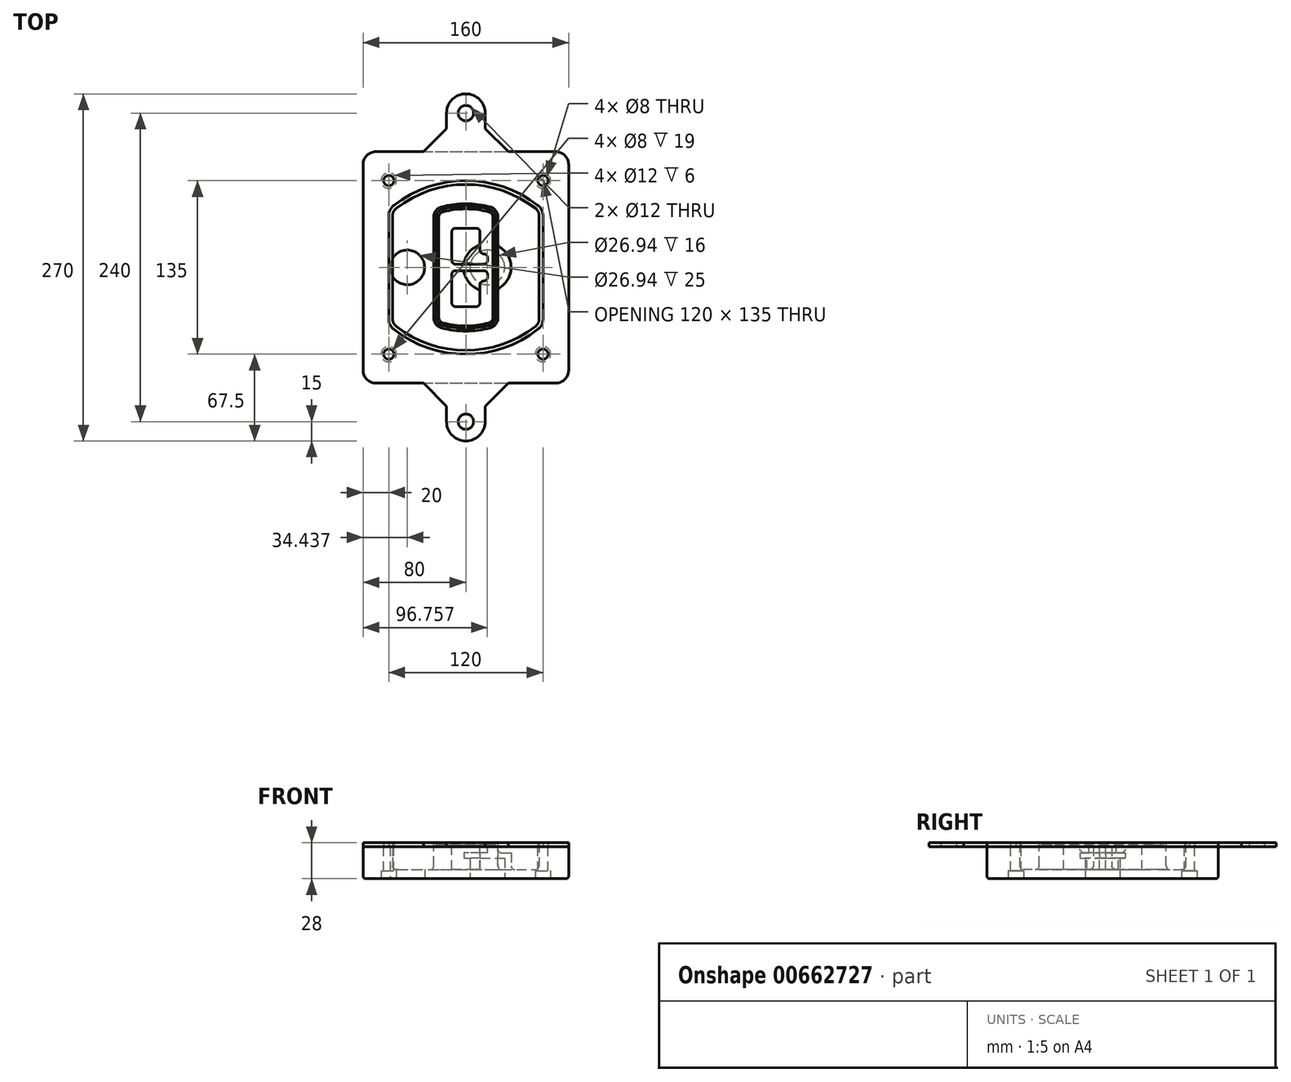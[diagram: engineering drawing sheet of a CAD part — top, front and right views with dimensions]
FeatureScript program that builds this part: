
annotation { "Feature Type Name" : "Feature", "Feature Type Description" : "" }
export const myFeature = defineFeature(function(context is Context, id is Id, definition is map)
    precondition{}
    {
        {
            var Q0;
            Q0=qCreatedBy(makeId("Top.planeOp"),FACE);
            var sketch = newSketch(context, id + "F0", { "sketchPlane" : qUnion([Q0])});
            skPoint(sketch, "E0.rect.middle", {"position": v(0, 0) * mm});
            skLineSegment(sketch, "E1.bottom", {"start": v(-70, -90) * mm, "end": v(70, -90) * mm});
            skLineSegment(sketch, "E1.top", {"start": v(-70, 90) * mm, "end": v(70, 90) * mm});
            skLineSegment(sketch, "E1.left", {"start": v(-80, -80) * mm, "end": v(-80, 80) * mm});
            skLineSegment(sketch, "E1.right", {"start": v(80, -80) * mm, "end": v(80, 80) * mm});
            skLineSegment(sketch, "E2", {"start": v(-80, 90) * mm, "end": v(80, -90) * mm, "construction": true});
            skLineSegment(sketch, "E3", {"start": v(80, 90) * mm, "end": v(-80, -90) * mm, "construction": true});
            skCircle(sketch, "E4", {"center": v(-60, 67.5) * mm, "radius": 4 * mm});
            skCircle(sketch, "E5", {"center": v(60, 67.5) * mm, "radius": 4 * mm});
            skCircle(sketch, "E6", {"center": v(60, -67.5) * mm, "radius": 4 * mm});
            skCircle(sketch, "E7", {"center": v(-60, -67.5) * mm, "radius": 4 * mm});
            skLineSegment(sketch, "E8", {"start": v(-60, 67.5) * mm, "end": v(60, 67.5) * mm, "construction": true});
            skLineSegment(sketch, "E9", {"start": v(60, 67.5) * mm, "end": v(60, -67.5) * mm, "construction": true});
            skLineSegment(sketch, "E10", {"start": v(60, -67.5) * mm, "end": v(-60, -67.5) * mm, "construction": true});
            skLineSegment(sketch, "E11", {"start": v(-60, -67.5) * mm, "end": v(-60, 67.5) * mm, "construction": true});
            skLineSegment(sketch, "E12", {"start": v(-60, 40.3) * mm, "end": v(-60, -40.3) * mm});
            skLineSegment(sketch, "E13", {"start": v(60, 40.3) * mm, "end": v(60, -40.3) * mm});
            skArc(sketch, "E14", {"start": v(56.15, 48.18) * mm, "mid": v(0, 67.5) * mm, "end": v(-56.15, 48.18) * mm});
            skArc(sketch, "E15", {"start": v(-56.15, -48.18) * mm, "mid": v(0, -67.5) * mm, "end": v(56.15, -48.18) * mm});
            skLineSegment(sketch, "E16", {"start": v(-60, 0) * mm, "end": v(60, 0) * mm, "construction": true});
            skPoint(sketch, "E17.visualSharp", {"position": v(-60, -45) * mm});
            skArc(sketch, "E17.filletArc", {"start": v(-60, -40.3) * mm, "mid": v(-58.99, -44.68) * mm, "end": v(-56.15, -48.18) * mm});
            skPoint(sketch, "E18.visualSharp", {"position": v(-60, 45) * mm});
            skArc(sketch, "E18.filletArc", {"start": v(-56.15, 48.18) * mm, "mid": v(-58.99, 44.68) * mm, "end": v(-60, 40.3) * mm});
            skPoint(sketch, "E19.visualSharp", {"position": v(60, 45) * mm});
            skArc(sketch, "E19.filletArc", {"start": v(60, 40.3) * mm, "mid": v(58.99, 44.68) * mm, "end": v(56.15, 48.18) * mm});
            skPoint(sketch, "E20.visualSharp", {"position": v(60, -45) * mm});
            skArc(sketch, "E20.filletArc", {"start": v(56.15, -48.18) * mm, "mid": v(58.99, -44.68) * mm, "end": v(60, -40.3) * mm});
            skPoint(sketch, "E21.visualSharp", {"position": v(-80, 90) * mm});
            skArc(sketch, "E21.filletArc", {"start": v(-70, 90) * mm, "mid": v(-77.07, 87.07) * mm, "end": v(-80, 80) * mm});
            skPoint(sketch, "E22.visualSharp", {"position": v(80, 90) * mm});
            skArc(sketch, "E22.filletArc", {"start": v(80, 80) * mm, "mid": v(77.07, 87.07) * mm, "end": v(70, 90) * mm});
            skPoint(sketch, "E23.visualSharp", {"position": v(80, -90) * mm});
            skArc(sketch, "E23.filletArc", {"start": v(70, -90) * mm, "mid": v(77.07, -87.07) * mm, "end": v(80, -80) * mm});
            skPoint(sketch, "E24.visualSharp", {"position": v(-80, -90) * mm});
            skArc(sketch, "E24.filletArc", {"start": v(-80, -80) * mm, "mid": v(-77.07, -87.07) * mm, "end": v(-70, -90) * mm});
            skArc(sketch, "E25.0", {"start": v(57, 40.3) * mm, "mid": v(56.3, 43.36) * mm, "end": v(54.3, 45.81) * mm});
            skLineSegment(sketch, "E25.1", {"start": v(57, 40.3) * mm, "end": v(57, -40.3) * mm});
            skArc(sketch, "E25.2", {"start": v(54.3, -45.81) * mm, "mid": v(56.3, -43.36) * mm, "end": v(57, -40.3) * mm});
            skArc(sketch, "E25.3", {"start": v(-54.3, -45.81) * mm, "mid": v(0, -64.5) * mm, "end": v(54.3, -45.81) * mm});
            skArc(sketch, "E25.4", {"start": v(-57, -40.3) * mm, "mid": v(-56.3, -43.36) * mm, "end": v(-54.3, -45.81) * mm});
            skArc(sketch, "E25.5", {"start": v(54.3, 45.81) * mm, "mid": v(0, 64.5) * mm, "end": v(-54.3, 45.81) * mm});
            skLineSegment(sketch, "E25.6", {"start": v(-57, 40.3) * mm, "end": v(-57, -40.3) * mm});
            skArc(sketch, "E25.7", {"start": v(-54.3, 45.81) * mm, "mid": v(-56.3, 43.36) * mm, "end": v(-57, 40.3) * mm});
            skArc(sketch, "E26.0", {"start": v(-58.62, 51.33) * mm, "mid": v(-62.58, 46.43) * mm, "end": v(-64, 40.3) * mm});
            skArc(sketch, "E26.1", {"start": v(58.62, 51.33) * mm, "mid": v(0, 71.5) * mm, "end": v(-58.62, 51.33) * mm});
            skArc(sketch, "E26.2", {"start": v(64, 40.3) * mm, "mid": v(62.58, 46.43) * mm, "end": v(58.62, 51.33) * mm});
            skLineSegment(sketch, "E26.3", {"start": v(64, 40.3) * mm, "end": v(64, -40.3) * mm});
            skArc(sketch, "E26.4", {"start": v(58.62, -51.33) * mm, "mid": v(62.58, -46.43) * mm, "end": v(64, -40.3) * mm});
            skLineSegment(sketch, "E26.5", {"start": v(-64, 40.3) * mm, "end": v(-64, -40.3) * mm});
            skArc(sketch, "E26.6", {"start": v(-58.62, -51.33) * mm, "mid": v(0, -71.5) * mm, "end": v(58.62, -51.33) * mm});
            skArc(sketch, "E26.7", {"start": v(-64, -40.3) * mm, "mid": v(-62.58, -46.43) * mm, "end": v(-58.62, -51.33) * mm});
            skSolve(sketch);
        }
        {
            var Q0;
            Q0=makeQuery(id+"F0.imprint","IMPRINT",FACE,{"disambiguationData":[TD([[makeQuery(id+"F0.imprint","IMPRINT",EDGE,{"derivedFrom":sQuery(id+"F0.wireOp",EDGE,"E1.bottom")}),1.0]])]});
            var Q1;
            Q1=makeQuery(id+"F0.imprint","IMPRINT",FACE,{"disambiguationData":[TD([[makeQuery(id+"F0.imprint","IMPRINT",EDGE,{"derivedFrom":sQuery(id+"F0.wireOp",EDGE,"E12")}),1.0]])]});
            var Q2;
            Q2=makeQuery(id+"F0.imprint","IMPRINT",FACE,{"disambiguationData":[TD([[makeQuery(id+"F0.imprint","IMPRINT",EDGE,{"derivedFrom":sQuery(id+"F0.wireOp",EDGE,"E25.0")}),1.0]])]});
            var Q3;
            Q3=makeQuery(id+"F0.imprint","IMPRINT",FACE,{"disambiguationData":[TD([[makeQuery(id+"F0.imprint","IMPRINT",EDGE,{"derivedFrom":sQuery(id+"F0.wireOp",EDGE,"E12")}),-1.0]])]});
            extrude(context, id + "F1", {"entities" : qUnion([Q0, Q1, Q2, Q3]), "oppositeDirection" : true, "depth" : 25 * mm});
        }
        {
            var Q0;
            Q0=makeQuery(id+"F0.imprint","IMPRINT",FACE,{"disambiguationData":[TD([[makeQuery(id+"F0.imprint","IMPRINT",EDGE,{"derivedFrom":sQuery(id+"F0.wireOp",EDGE,"E12")}),1.0]])]});
            extrude(context, id + "F2", {"entities" : qUnion([Q0]), "operationType" : NewBodyOperationType.ADD, "depth" : 3 * mm});
        }
        {
            var Q0;
            Q0=makeQuery(id+"F0.imprint","IMPRINT",FACE,{"disambiguationData":[TD([[makeQuery(id+"F0.imprint","IMPRINT",EDGE,{"derivedFrom":sQuery(id+"F0.wireOp",EDGE,"E25.0")}),1.0]])]});
            extrude(context, id + "F3", {"entities" : qUnion([Q0]), "operationType" : NewBodyOperationType.REMOVE, "oppositeDirection" : true, "depth" : 18 * mm});
        }
        {
            var Q0;
            Q0=makeQuery(id+"F2.opExtrude","CAP_FACE",FACE,{"disambiguationData":[OSD([sQuery(id+"F0.wireOp",EDGE,"E12"),sQuery(id+"F0.wireOp",EDGE,"E13"),sQuery(id+"F0.wireOp",EDGE,"E14"),sQuery(id+"F0.wireOp",EDGE,"E15"),sQuery(id+"F0.wireOp",EDGE,"E17.filletArc"),sQuery(id+"F0.wireOp",EDGE,"E18.filletArc"),sQuery(id+"F0.wireOp",EDGE,"E19.filletArc"),sQuery(id+"F0.wireOp",EDGE,"E20.filletArc"),sQuery(id+"F0.wireOp",EDGE,"E25.0"),sQuery(id+"F0.wireOp",EDGE,"E25.1"),sQuery(id+"F0.wireOp",EDGE,"E25.2"),sQuery(id+"F0.wireOp",EDGE,"E25.3"),sQuery(id+"F0.wireOp",EDGE,"E25.4"),sQuery(id+"F0.wireOp",EDGE,"E25.5"),sQuery(id+"F0.wireOp",EDGE,"E25.6"),sQuery(id+"F0.wireOp",EDGE,"E25.7")])],"isStart":false});
            var sketch = newSketch(context, id + "F4", { "sketchPlane" : qUnion([Q0])});
            skArc(sketch, "E27.0", {"start": v(-19.08, -46.97) * mm, "mid": v(0, -49.5) * mm, "end": v(19.08, -46.97) * mm});
            skArc(sketch, "E28.0", {"start": v(19.08, 46.97) * mm, "mid": v(0, 49.5) * mm, "end": v(-19.08, 46.97) * mm});
            skLineSegment(sketch, "E29", {"start": v(-25, 39.25) * mm, "end": v(-25, -39.25) * mm});
            skLineSegment(sketch, "E30", {"start": v(25, 39.25) * mm, "end": v(25, -39.25) * mm});
            skLineSegment(sketch, "E31", {"start": v(-25, 45.1) * mm, "end": v(25, 45.1) * mm, "construction": true});
            skLineSegment(sketch, "E32", {"start": v(-25, -45.1) * mm, "end": v(25, -45.1) * mm, "construction": true});
            skPoint(sketch, "E33.visualSharp", {"position": v(-25, 45.1) * mm});
            skArc(sketch, "E33.filletArc", {"start": v(-19.08, 46.97) * mm, "mid": v(-23.35, 44.11) * mm, "end": v(-25, 39.25) * mm});
            skPoint(sketch, "E34.visualSharp", {"position": v(25, 45.1) * mm});
            skArc(sketch, "E34.filletArc", {"start": v(25, 39.25) * mm, "mid": v(23.35, 44.11) * mm, "end": v(19.08, 46.97) * mm});
            skPoint(sketch, "E35.visualSharp", {"position": v(25, -45.1) * mm});
            skArc(sketch, "E35.filletArc", {"start": v(19.08, -46.97) * mm, "mid": v(23.35, -44.11) * mm, "end": v(25, -39.25) * mm});
            skPoint(sketch, "E36.visualSharp", {"position": v(-25, -45.1) * mm});
            skArc(sketch, "E36.filletArc", {"start": v(-25, -39.25) * mm, "mid": v(-23.35, -44.11) * mm, "end": v(-19.08, -46.97) * mm});
            skArc(sketch, "E37.0", {"start": v(54.3, 45.81) * mm, "mid": v(0, 64.5) * mm, "end": v(-54.3, 45.81) * mm});
            skArc(sketch, "E37.1", {"start": v(-54.3, 45.81) * mm, "mid": v(-56.3, 43.36) * mm, "end": v(-57, 40.3) * mm});
            skLineSegment(sketch, "E37.2", {"start": v(-57, 40.3) * mm, "end": v(-57, -40.3) * mm});
            skArc(sketch, "E37.3", {"start": v(-57, -40.3) * mm, "mid": v(-56.3, -43.36) * mm, "end": v(-54.3, -45.81) * mm});
            skArc(sketch, "E37.4", {"start": v(-54.3, -45.81) * mm, "mid": v(0, -64.5) * mm, "end": v(54.3, -45.81) * mm});
            skArc(sketch, "E37.5", {"start": v(54.3, -45.81) * mm, "mid": v(56.3, -43.36) * mm, "end": v(57, -40.3) * mm});
            skLineSegment(sketch, "E37.6", {"start": v(57, 40.3) * mm, "end": v(57, -40.3) * mm});
            skArc(sketch, "E37.7", {"start": v(57, 40.3) * mm, "mid": v(56.3, 43.36) * mm, "end": v(54.3, 45.81) * mm});
            skLineSegment(sketch, "E38.0", {"start": v(23, 39.25) * mm, "end": v(23, -39.25) * mm});
            skArc(sketch, "E38.1", {"start": v(18.56, -45.04) * mm, "mid": v(21.76, -42.9) * mm, "end": v(23, -39.25) * mm});
            skArc(sketch, "E38.2", {"start": v(-18.56, -45.04) * mm, "mid": v(0, -47.5) * mm, "end": v(18.56, -45.04) * mm});
            skArc(sketch, "E38.3", {"start": v(-23, -39.25) * mm, "mid": v(-21.76, -42.9) * mm, "end": v(-18.56, -45.04) * mm});
            skLineSegment(sketch, "E38.4", {"start": v(-23, 39.25) * mm, "end": v(-23, -39.25) * mm});
            skArc(sketch, "E38.5", {"start": v(23, 39.25) * mm, "mid": v(21.76, 42.9) * mm, "end": v(18.56, 45.04) * mm});
            skArc(sketch, "E38.6", {"start": v(-18.56, 45.04) * mm, "mid": v(-21.76, 42.9) * mm, "end": v(-23, 39.25) * mm});
            skArc(sketch, "E38.7", {"start": v(18.56, 45.04) * mm, "mid": v(0, 47.5) * mm, "end": v(-18.56, 45.04) * mm});
            skArc(sketch, "E39.0", {"start": v(21, 39.25) * mm, "mid": v(20.18, 41.68) * mm, "end": v(18.04, 43.1) * mm});
            skLineSegment(sketch, "E39.1", {"start": v(21, 39.25) * mm, "end": v(21, -39.25) * mm});
            skArc(sketch, "E39.2", {"start": v(18.04, -43.1) * mm, "mid": v(20.18, -41.68) * mm, "end": v(21, -39.25) * mm});
            skArc(sketch, "E39.3", {"start": v(-18.04, -43.1) * mm, "mid": v(0, -45.5) * mm, "end": v(18.04, -43.1) * mm});
            skArc(sketch, "E39.4", {"start": v(-21, -39.25) * mm, "mid": v(-20.18, -41.68) * mm, "end": v(-18.04, -43.1) * mm});
            skArc(sketch, "E39.5", {"start": v(18.04, 43.1) * mm, "mid": v(0, 45.5) * mm, "end": v(-18.04, 43.1) * mm});
            skLineSegment(sketch, "E39.6", {"start": v(-21, 39.25) * mm, "end": v(-21, -39.25) * mm});
            skArc(sketch, "E39.7", {"start": v(-18.04, 43.1) * mm, "mid": v(-20.18, 41.68) * mm, "end": v(-21, 39.25) * mm});
            skLineSegment(sketch, "E40", {"start": v(-25, 0) * mm, "end": v(25, 0) * mm, "construction": true});
            skLineSegment(sketch, "E41", {"start": v(-11, 5.5) * mm, "end": v(-11, 27.5) * mm});
            skLineSegment(sketch, "E42", {"start": v(-8, 30.5) * mm, "end": v(8, 30.5) * mm});
            skLineSegment(sketch, "E43", {"start": v(11, 27.5) * mm, "end": v(11, 13.5) * mm});
            skLineSegment(sketch, "E44", {"start": v(14, 10.5) * mm, "end": v(14, 10.5) * mm});
            skLineSegment(sketch, "E45", {"start": v(17, 7.5) * mm, "end": v(17, 5.5) * mm});
            skLineSegment(sketch, "E46", {"start": v(14, 2.5) * mm, "end": v(-8, 2.5) * mm});
            skPoint(sketch, "E47.visualSharp", {"position": v(-11, 30.5) * mm});
            skArc(sketch, "E47.filletArc", {"start": v(-8, 30.5) * mm, "mid": v(-10.12, 29.62) * mm, "end": v(-11, 27.5) * mm});
            skPoint(sketch, "E48.visualSharp", {"position": v(11, 30.5) * mm});
            skArc(sketch, "E48.filletArc", {"start": v(11, 27.5) * mm, "mid": v(10.12, 29.62) * mm, "end": v(8, 30.5) * mm});
            skPoint(sketch, "E49.visualSharp", {"position": v(11, 10.5) * mm});
            skArc(sketch, "E49.filletArc", {"start": v(11, 13.5) * mm, "mid": v(11.88, 11.38) * mm, "end": v(14, 10.5) * mm});
            skPoint(sketch, "E50.visualSharp", {"position": v(17, 10.5) * mm});
            skArc(sketch, "E50.filletArc", {"start": v(17, 7.5) * mm, "mid": v(16.12, 9.62) * mm, "end": v(14, 10.5) * mm});
            skPoint(sketch, "E51.visualSharp", {"position": v(17, 2.5) * mm});
            skArc(sketch, "E51.filletArc", {"start": v(14, 2.5) * mm, "mid": v(16.12, 3.38) * mm, "end": v(17, 5.5) * mm});
            skPoint(sketch, "E52.visualSharp", {"position": v(-11, 2.5) * mm});
            skArc(sketch, "E52.filletArc", {"start": v(-11, 5.5) * mm, "mid": v(-10.12, 3.38) * mm, "end": v(-8, 2.5) * mm});
            skLineSegment(sketch, "E53.0.MirrorCS", {"start": v(14, -2.5) * mm, "end": v(-8, -2.5) * mm});
            skArc(sketch, "E54.0.MirrorCS", {"start": v(-11, -5.5) * mm, "mid": v(-10.12, -3.38) * mm, "end": v(-8, -2.5) * mm});
            skLineSegment(sketch, "E55.0.MirrorCS", {"start": v(-11, -5.5) * mm, "end": v(-11, -27.5) * mm});
            skArc(sketch, "E56.0.MirrorCS", {"start": v(-8, -30.5) * mm, "mid": v(-10.12, -29.62) * mm, "end": v(-11, -27.5) * mm});
            skLineSegment(sketch, "E57.0.MirrorCS", {"start": v(-8, -30.5) * mm, "end": v(8, -30.5) * mm});
            skArc(sketch, "E58.0.MirrorCS", {"start": v(11, -27.5) * mm, "mid": v(10.12, -29.62) * mm, "end": v(8, -30.5) * mm});
            skLineSegment(sketch, "E59.0.MirrorCS", {"start": v(11, -27.5) * mm, "end": v(11, -13.5) * mm});
            skArc(sketch, "E60.0.MirrorCS", {"start": v(11, -13.5) * mm, "mid": v(11.88, -11.38) * mm, "end": v(14, -10.5) * mm});
            skArc(sketch, "E61.0.MirrorCS", {"start": v(17, -7.5) * mm, "mid": v(16.12, -9.62) * mm, "end": v(14, -10.5) * mm});
            skLineSegment(sketch, "E62.0.MirrorCS", {"start": v(17, -7.5) * mm, "end": v(17, -5.5) * mm});
            skArc(sketch, "E63.0.MirrorCS", {"start": v(14, -2.5) * mm, "mid": v(16.12, -3.38) * mm, "end": v(17, -5.5) * mm});
            skSolve(sketch);
        }
        {
            var Q0;
            Q0=makeQuery(id+"F4.imprint","IMPRINT",FACE,{"disambiguationData":[TD([[makeQuery(id+"F4.imprint","IMPRINT",EDGE,{"derivedFrom":sQuery(id+"F4.wireOp",EDGE,"E27.0")}),1.0]])]});
            var Q1;
            Q1=makeQuery(id+"F4.imprint","IMPRINT",FACE,{"disambiguationData":[TD([[makeQuery(id+"F4.imprint","IMPRINT",EDGE,{"derivedFrom":sQuery(id+"F4.wireOp",EDGE,"E38.0")}),-1.0]])]});
            var Q2;
            Q2=makeQuery(id+"F4.imprint","IMPRINT",FACE,{"disambiguationData":[TD([[makeQuery(id+"F4.imprint","IMPRINT",EDGE,{"derivedFrom":sQuery(id+"F4.wireOp",EDGE,"E39.0")}),1.0]])]});
            extrude(context, id + "F5", {"entities" : qUnion([Q0, Q1, Q2]), "operationType" : NewBodyOperationType.ADD, "endBound" : BoundingType.UP_TO_NEXT, "oppositeDirection" : true, "depth" : 25 * mm});
        }
        {
            var Q0;
            Q0=makeQuery(id+"F4.imprint","IMPRINT",FACE,{"disambiguationData":[TD([[makeQuery(id+"F4.imprint","IMPRINT",EDGE,{"derivedFrom":sQuery(id+"F4.wireOp",EDGE,"E38.0")}),-1.0]])]});
            extrude(context, id + "F6", {"entities" : qUnion([Q0]), "operationType" : NewBodyOperationType.REMOVE, "oppositeDirection" : true, "depth" : 2 * mm});
        }
        {
            var Q0;
            Q0=makeQuery(id+"F1.opExtrude","CAP_FACE",FACE,{"disambiguationData":[OSD([sQuery(id+"F0.wireOp",EDGE,"E1.bottom"),sQuery(id+"F0.wireOp",EDGE,"E1.top"),sQuery(id+"F0.wireOp",EDGE,"E1.left"),sQuery(id+"F0.wireOp",EDGE,"E1.right"),sQuery(id+"F0.wireOp",EDGE,"E4"),sQuery(id+"F0.wireOp",EDGE,"E5"),sQuery(id+"F0.wireOp",EDGE,"E6"),sQuery(id+"F0.wireOp",EDGE,"E7"),sQuery(id+"F0.wireOp",EDGE,"E21.filletArc"),sQuery(id+"F0.wireOp",EDGE,"E22.filletArc"),sQuery(id+"F0.wireOp",EDGE,"E23.filletArc"),sQuery(id+"F0.wireOp",EDGE,"E24.filletArc")])],"isStart":false});
            var sketch = newSketch(context, id + "F7", { "sketchPlane" : qUnion([Q0])});
            skCircle(sketch, "E64", {"center": v(16.76, 0) * mm, "radius": 13.47 * mm});
            skCircle(sketch, "E65", {"center": v(-45.56, 0) * mm, "radius": 13.47 * mm});
            skLineSegment(sketch, "E66", {"start": v(80, 0) * mm, "end": v(-80, 0) * mm});
            skCircle(sketch, "E67", {"center": v(16.76, 0) * mm, "radius": 18.47 * mm});
            skCircle(sketch, "E68", {"center": v(60, -67.5) * mm, "radius": 6 * mm});
            skCircle(sketch, "E69", {"center": v(-60, -67.5) * mm, "radius": 6 * mm});
            skCircle(sketch, "E70", {"center": v(-60, 67.5) * mm, "radius": 6 * mm});
            skCircle(sketch, "E71", {"center": v(60, 67.5) * mm, "radius": 6 * mm});
            skSolve(sketch);
        }
        {
            var Q0;
            {var subQ1=sQuery(id+"F7.wireOp",EDGE,"E66");var subQ4=sQuery(id+"F7.wireOp",EDGE,"E64");var subQ6=makeQuery(id+"F7.imprint","INTERSECT",VERTEX,{"disambiguationData":[OD(0.0)],"derivedFrom":[subQ4,subQ1]});Q0=makeQuery(id+"F7.imprint","IMPRINT",FACE,{"disambiguationData":[TD([[makeQuery(id+"F7.imprint","IMPRINT",EDGE,{"disambiguationData":[TD([[subQ6,-1.0]])],"derivedFrom":subQ4}),-1.0]])]});}
            var Q1;
            {var subQ0=sQuery(id+"F7.wireOp",EDGE,"E66");var subQ1=sQuery(id+"F7.wireOp",EDGE,"E64");var subQ3=makeQuery(id+"F7.imprint","INTERSECT",VERTEX,{"disambiguationData":[OD(0.0)],"derivedFrom":[subQ1,subQ0]});Q1=makeQuery(id+"F7.imprint","IMPRINT",FACE,{"disambiguationData":[TD([[makeQuery(id+"F7.imprint","IMPRINT",EDGE,{"disambiguationData":[TD([[subQ3,-1.0]])],"derivedFrom":subQ1}),1.0]])]});}
            var Q2;
            {var subQ0=sQuery(id+"F7.wireOp",EDGE,"E66");var subQ1=sQuery(id+"F7.wireOp",EDGE,"E64");var subQ3=makeQuery(id+"F7.imprint","INTERSECT",VERTEX,{"disambiguationData":[OD(0.0)],"derivedFrom":[subQ1,subQ0]});Q2=makeQuery(id+"F7.imprint","IMPRINT",FACE,{"disambiguationData":[TD([[makeQuery(id+"F7.imprint","IMPRINT",EDGE,{"disambiguationData":[TD([[subQ3,1.0]])],"derivedFrom":subQ1}),1.0]])]});}
            var Q3;
            {var subQ1=sQuery(id+"F7.wireOp",EDGE,"E66");var subQ4=sQuery(id+"F7.wireOp",EDGE,"E64");var subQ6=makeQuery(id+"F7.imprint","INTERSECT",VERTEX,{"disambiguationData":[OD(0.0)],"derivedFrom":[subQ4,subQ1]});Q3=makeQuery(id+"F7.imprint","IMPRINT",FACE,{"disambiguationData":[TD([[makeQuery(id+"F7.imprint","IMPRINT",EDGE,{"disambiguationData":[TD([[subQ6,1.0]])],"derivedFrom":subQ4}),-1.0]])]});}
            extrude(context, id + "F8", {"entities" : qUnion([Q0, Q1, Q2, Q3]), "operationType" : NewBodyOperationType.ADD, "oppositeDirection" : true, "depth" : 20 * mm});
        }
        {
            var Q0;
            {var subQ0=sQuery(id+"F7.wireOp",EDGE,"E66");var subQ1=sQuery(id+"F7.wireOp",EDGE,"E64");var subQ3=makeQuery(id+"F7.imprint","INTERSECT",VERTEX,{"disambiguationData":[OD(0.0)],"derivedFrom":[subQ1,subQ0]});Q0=makeQuery(id+"F7.imprint","IMPRINT",FACE,{"disambiguationData":[TD([[makeQuery(id+"F7.imprint","IMPRINT",EDGE,{"disambiguationData":[TD([[subQ3,-1.0]])],"derivedFrom":subQ1}),1.0]])]});}
            var Q1;
            {var subQ0=sQuery(id+"F7.wireOp",EDGE,"E66");var subQ1=sQuery(id+"F7.wireOp",EDGE,"E64");var subQ3=makeQuery(id+"F7.imprint","INTERSECT",VERTEX,{"disambiguationData":[OD(0.0)],"derivedFrom":[subQ1,subQ0]});Q1=makeQuery(id+"F7.imprint","IMPRINT",FACE,{"disambiguationData":[TD([[makeQuery(id+"F7.imprint","IMPRINT",EDGE,{"disambiguationData":[TD([[subQ3,1.0]])],"derivedFrom":subQ1}),1.0]])]});}
            extrude(context, id + "F9", {"entities" : qUnion([Q0, Q1]), "operationType" : NewBodyOperationType.REMOVE, "oppositeDirection" : true, "depth" : 16 * mm});
        }
        {
            var Q0;
            {var subQ0=sQuery(id+"F7.wireOp",EDGE,"E66");var subQ1=sQuery(id+"F7.wireOp",EDGE,"E65");var subQ3=makeQuery(id+"F7.imprint","INTERSECT",VERTEX,{"disambiguationData":[OD(0.0)],"derivedFrom":[subQ1,subQ0]});Q0=makeQuery(id+"F7.imprint","IMPRINT",FACE,{"disambiguationData":[TD([[makeQuery(id+"F7.imprint","IMPRINT",EDGE,{"disambiguationData":[TD([[subQ3,-1.0]])],"derivedFrom":subQ1}),1.0]])]});}
            var Q1;
            {var subQ0=sQuery(id+"F7.wireOp",EDGE,"E66");var subQ1=sQuery(id+"F7.wireOp",EDGE,"E65");var subQ3=makeQuery(id+"F7.imprint","INTERSECT",VERTEX,{"disambiguationData":[OD(0.0)],"derivedFrom":[subQ1,subQ0]});Q1=makeQuery(id+"F7.imprint","IMPRINT",FACE,{"disambiguationData":[TD([[makeQuery(id+"F7.imprint","IMPRINT",EDGE,{"disambiguationData":[TD([[subQ3,1.0]])],"derivedFrom":subQ1}),1.0]])]});}
            extrude(context, id + "F10", {"entities" : qUnion([Q0, Q1]), "operationType" : NewBodyOperationType.REMOVE, "oppositeDirection" : true, "depth" : 25 * mm});
        }
        {
            var Q0;
            Q0=makeQuery(id+"F7.imprint","IMPRINT",FACE,{"disambiguationData":[TD([[makeQuery(id+"F7.imprint","IMPRINT",EDGE,{"derivedFrom":sQuery(id+"F7.wireOp",EDGE,"E68")}),1.0]])]});
            var Q1;
            Q1=makeQuery(id+"F7.imprint","IMPRINT",FACE,{"disambiguationData":[TD([[makeQuery(id+"F7.imprint","IMPRINT",EDGE,{"derivedFrom":makeQuery(id+"F1.opExtrude","CAP_EDGE",EDGE,{"disambiguationData":[OSD([sQuery(id+"F0.wireOp",EDGE,"E5")])],"isStart":false})}),-1.0]])]});
            var Q2;
            Q2=makeQuery(id+"F7.imprint","IMPRINT",FACE,{"disambiguationData":[TD([[makeQuery(id+"F7.imprint","IMPRINT",EDGE,{"derivedFrom":sQuery(id+"F7.wireOp",EDGE,"E69")}),1.0]])]});
            var Q3;
            Q3=makeQuery(id+"F7.imprint","IMPRINT",FACE,{"disambiguationData":[TD([[makeQuery(id+"F7.imprint","IMPRINT",EDGE,{"derivedFrom":makeQuery(id+"F1.opExtrude","CAP_EDGE",EDGE,{"disambiguationData":[OSD([sQuery(id+"F0.wireOp",EDGE,"E4")])],"isStart":false})}),-1.0]])]});
            var Q4;
            Q4=makeQuery(id+"F7.imprint","IMPRINT",FACE,{"disambiguationData":[TD([[makeQuery(id+"F7.imprint","IMPRINT",EDGE,{"derivedFrom":sQuery(id+"F7.wireOp",EDGE,"E70")}),1.0]])]});
            var Q5;
            Q5=makeQuery(id+"F7.imprint","IMPRINT",FACE,{"disambiguationData":[TD([[makeQuery(id+"F7.imprint","IMPRINT",EDGE,{"derivedFrom":makeQuery(id+"F1.opExtrude","CAP_EDGE",EDGE,{"disambiguationData":[OSD([sQuery(id+"F0.wireOp",EDGE,"E7")])],"isStart":false})}),-1.0]])]});
            var Q6;
            Q6=makeQuery(id+"F7.imprint","IMPRINT",FACE,{"disambiguationData":[TD([[makeQuery(id+"F7.imprint","IMPRINT",EDGE,{"derivedFrom":sQuery(id+"F7.wireOp",EDGE,"E71")}),1.0]])]});
            var Q7;
            Q7=makeQuery(id+"F7.imprint","IMPRINT",FACE,{"disambiguationData":[TD([[makeQuery(id+"F7.imprint","IMPRINT",EDGE,{"derivedFrom":makeQuery(id+"F1.opExtrude","CAP_EDGE",EDGE,{"disambiguationData":[OSD([sQuery(id+"F0.wireOp",EDGE,"E6")])],"isStart":false})}),-1.0]])]});
            extrude(context, id + "F11", {"entities" : qUnion([Q0, Q1, Q2, Q3, Q4, Q5, Q6, Q7]), "operationType" : NewBodyOperationType.REMOVE, "oppositeDirection" : true, "depth" : 6 * mm});
        }
        {
            var Q0;
            Q0=makeQuery(id+"F9.boolean.opBoolean","COPY",FACE,{"derivedFrom":makeQuery(id+"F9.opExtrude","CAP_FACE",FACE,{"disambiguationData":[OSD([sQuery(id+"F7.wireOp",EDGE,"E64")])],"isStart":false})});
            var sketch = newSketch(context, id + "F12", { "sketchPlane" : qUnion([Q0])});
            skArc(sketch, "E72.0", {"start": v(11, 17.55) * mm, "mid": v(2.57, 11.82) * mm, "end": v(-1.54, 2.5) * mm});
            skArc(sketch, "E72.1", {"start": v(-1.54, -2.5) * mm, "mid": v(2.57, -11.82) * mm, "end": v(11, -17.55) * mm});
            skLineSegment(sketch, "E73", {"start": v(-1.54, -2.5) * mm, "end": v(14, -2.5) * mm});
            skLineSegment(sketch, "E74.0", {"start": v(14, 2.5) * mm, "end": v(-1.54, 2.5) * mm});
            skArc(sketch, "E74.1", {"start": v(14, 2.5) * mm, "mid": v(16.12, 3.38) * mm, "end": v(17, 5.5) * mm});
            skLineSegment(sketch, "E74.2", {"start": v(17, 7.5) * mm, "end": v(17, 5.5) * mm});
            skArc(sketch, "E74.3", {"start": v(17, 7.5) * mm, "mid": v(16.12, 9.62) * mm, "end": v(14, 10.5) * mm});
            skArc(sketch, "E74.4", {"start": v(11, 13.5) * mm, "mid": v(11.88, 11.38) * mm, "end": v(14, 10.5) * mm});
            skLineSegment(sketch, "E74.5", {"start": v(11, 17.55) * mm, "end": v(11, 13.5) * mm});
            skLineSegment(sketch, "E74.7", {"start": v(14, -2.5) * mm, "end": v(-1.54, -2.5) * mm});
            skArc(sketch, "E74.8", {"start": v(14, -2.5) * mm, "mid": v(16.12, -3.38) * mm, "end": v(17, -5.5) * mm});
            skLineSegment(sketch, "E74.9", {"start": v(17, -7.5) * mm, "end": v(17, -5.5) * mm});
            skArc(sketch, "E74.10", {"start": v(17, -7.5) * mm, "mid": v(16.12, -9.62) * mm, "end": v(14, -10.5) * mm});
            skArc(sketch, "E74.11", {"start": v(11, -13.5) * mm, "mid": v(11.88, -11.38) * mm, "end": v(14, -10.5) * mm});
            skLineSegment(sketch, "E74.12", {"start": v(11, -17.55) * mm, "end": v(11, -13.5) * mm});
            skPoint(sketch, "E75.orphan", {"position": v(11, -27.5) * mm});
            skPoint(sketch, "E76.orphan", {"position": v(-8, -2.5) * mm});
            skPoint(sketch, "E77.orphan", {"position": v(-8, 2.5) * mm});
            skPoint(sketch, "E78.orphan", {"position": v(11, 27.5) * mm});
            skSolve(sketch);
        }
        {
            var Q0;
            {var subQ7=sQuery(id+"F12.wireOp",EDGE,"E72.0");var subQ14=sQuery(id+"F12.wireOp",EDGE,"E72.1");var subQ16=sQuery(id+"F12.wireOp",EDGE,"E74.1");var subQ18=sQuery(id+"F12.wireOp",EDGE,"E74.8");Q0=qUnion([makeQuery(id+"F12.imprint","IMPRINT",FACE,{"disambiguationData":[TD([[makeQuery(id+"F12.imprint","IMPRINT",EDGE,{"derivedFrom":subQ7}),1.0]])]}),makeQuery(id+"F12.imprint","IMPRINT",FACE,{"disambiguationData":[TD([[makeQuery(id+"F12.imprint","IMPRINT",EDGE,{"derivedFrom":subQ14}),1.0]])]}),makeQuery(id+"F12.imprint","IMPRINT",FACE,{"disambiguationData":[TD([[makeQuery(id+"F12.imprint","IMPRINT",EDGE,{"derivedFrom":subQ16}),1.0]])]}),makeQuery(id+"F12.imprint","IMPRINT",FACE,{"disambiguationData":[TD([[makeQuery(id+"F12.imprint","IMPRINT",EDGE,{"derivedFrom":subQ18}),-1.0]])]})]);}
            var Q1;
            Q1=makeQuery(id+"F5.boolean.opBoolean","SPLIT",FACE,{"disambiguationData":[TD([makeQuery(id+"F5.opExtrude","SWEPT_FACE",FACE,{"disambiguationData":[OSD([sQuery(id+"F4.wireOp",EDGE,"E41")])]})])],"derivedFrom":makeQuery(id+"F3.boolean.opBoolean","COPY",FACE,{"derivedFrom":makeQuery(id+"F3.opExtrude","CAP_FACE",FACE,{"disambiguationData":[OSD([sQuery(id+"F0.wireOp",EDGE,"E25.0"),sQuery(id+"F0.wireOp",EDGE,"E25.1"),sQuery(id+"F0.wireOp",EDGE,"E25.2"),sQuery(id+"F0.wireOp",EDGE,"E25.3"),sQuery(id+"F0.wireOp",EDGE,"E25.4"),sQuery(id+"F0.wireOp",EDGE,"E25.5"),sQuery(id+"F0.wireOp",EDGE,"E25.6"),sQuery(id+"F0.wireOp",EDGE,"E25.7")])],"isStart":false})})});
            extrude(context, id + "F13", {"entities" : qUnion([Q0]), "operationType" : NewBodyOperationType.REMOVE, "endBound" : BoundingType.UP_TO_SURFACE, "endBoundEntityFace" : qUnion([Q1]), "depth" : 25 * mm});
        }
        {
            var Q0;
            Q0=makeQuery(id+"F3.boolean.opBoolean","COPY",EDGE,{"derivedFrom":makeQuery(id+"F3.opExtrude","CAP_EDGE",EDGE,{"disambiguationData":[OSD([sQuery(id+"F0.wireOp",EDGE,"E25.6")])],"isStart":false})});
            var Q1;
            Q1=makeQuery(id+"F8.boolean.opBoolean","INTERSECT",EDGE,{"derivedFrom":[makeQuery(id+"F5.opExtrude","SWEPT_FACE",FACE,{"disambiguationData":[OSD([sQuery(id+"F4.wireOp",EDGE,"E30")])]}),makeQuery(id+"F8.opExtrude","CAP_FACE",FACE,{"disambiguationData":[OSD([sQuery(id+"F7.wireOp",EDGE,"E67")])],"isStart":false})]});
            var Q2;
            Q2=makeQuery(id+"F8.boolean.opBoolean","INTERSECT",EDGE,{"disambiguationData":[OD(1.0)],"derivedFrom":[makeQuery(id+"F5.opExtrude","SWEPT_FACE",FACE,{"disambiguationData":[OSD([sQuery(id+"F4.wireOp",EDGE,"E30")])]}),makeQuery(id+"F8.opExtrude","SWEPT_FACE",FACE,{"disambiguationData":[OSD([sQuery(id+"F7.wireOp",EDGE,"E67")])]})]});
            var Q3;
            {var subQ0=sQuery(id+"F4.wireOp",EDGE,"E30");Q3=makeQuery(id+"F8.boolean.opBoolean","SPLIT",EDGE,{"disambiguationData":[TD([makeQuery(id+"F5.opExtrude","SWEPT_FACE",FACE,{"disambiguationData":[OSD([sQuery(id+"F4.wireOp",EDGE,"E35.filletArc")])]})])],"derivedFrom":makeQuery(id+"F5.opExtrude","CAP_EDGE",EDGE,{"disambiguationData":[OSD([subQ0])],"isStart":false})});}
            var Q4;
            {var subQ0=sQuery(id+"F0.wireOp",EDGE,"E25.7");var subQ1=sQuery(id+"F0.wireOp",EDGE,"E25.1");var subQ2=sQuery(id+"F0.wireOp",EDGE,"E25.6");var subQ3=sQuery(id+"F0.wireOp",EDGE,"E25.5");var subQ4=sQuery(id+"F0.wireOp",EDGE,"E25.4");var subQ5=sQuery(id+"F0.wireOp",EDGE,"E25.0");var subQ6=sQuery(id+"F0.wireOp",EDGE,"E25.2");var subQ7=sQuery(id+"F0.wireOp",EDGE,"E25.3");Q4=makeQuery(id+"F8.boolean.opBoolean","INTERSECT",EDGE,{"derivedFrom":[makeQuery(id+"F5.boolean.opBoolean","SPLIT",FACE,{"disambiguationData":[TD([makeQuery(id+"F2.opExtrude","SWEPT_FACE",FACE,{"disambiguationData":[OSD([subQ5])]})])],"derivedFrom":makeQuery(id+"F3.boolean.opBoolean","COPY",FACE,{"derivedFrom":makeQuery(id+"F3.opExtrude","CAP_FACE",FACE,{"disambiguationData":[OSD([subQ5,subQ1,subQ6,subQ7,subQ4,subQ3,subQ2,subQ0])],"isStart":false})})}),makeQuery(id+"F8.opExtrude","SWEPT_FACE",FACE,{"disambiguationData":[OSD([sQuery(id+"F7.wireOp",EDGE,"E67")])]})]});}
            var Q5;
            Q5=makeQuery(id+"F8.boolean.opBoolean","INTERSECT",EDGE,{"disambiguationData":[OD(0.0)],"derivedFrom":[makeQuery(id+"F5.opExtrude","SWEPT_FACE",FACE,{"disambiguationData":[OSD([sQuery(id+"F4.wireOp",EDGE,"E30")])]}),makeQuery(id+"F8.opExtrude","SWEPT_FACE",FACE,{"disambiguationData":[OSD([sQuery(id+"F7.wireOp",EDGE,"E67")])]})]});
            fillet(context, id + "F14", {"entities" : qUnion([Q0, Q1, Q2, Q3, Q4, Q5]), "radius" : 3 * mm, "tangentPropagation" : true, "allowEdgeOverflow" : false});
        }
        {
            var Q0;
            Q0=makeQuery(id+"F1.opExtrude","CAP_EDGE",EDGE,{"disambiguationData":[OSD([sQuery(id+"F0.wireOp",EDGE,"E1.bottom")])],"isStart":false});
            fillet(context, id + "F15", {"entities" : qUnion([Q0]), "radius" : 2 * mm, "tangentPropagation" : true, "allowEdgeOverflow" : false});
        }
        {
            var Q0;
            {var subQ0=sQuery(id+"F0.wireOp",EDGE,"E21.filletArc");var subQ1=sQuery(id+"F0.wireOp",EDGE,"E7");var subQ2=sQuery(id+"F0.wireOp",EDGE,"E6");var subQ3=sQuery(id+"F0.wireOp",EDGE,"E5");var subQ4=sQuery(id+"F0.wireOp",EDGE,"E4");var subQ5=sQuery(id+"F0.wireOp",EDGE,"E22.filletArc");var subQ6=sQuery(id+"F0.wireOp",EDGE,"E1.bottom");var subQ7=sQuery(id+"F0.wireOp",EDGE,"E1.right");var subQ8=sQuery(id+"F0.wireOp",EDGE,"E1.top");var subQ9=sQuery(id+"F0.wireOp",EDGE,"E1.left");var subQ10=sQuery(id+"F0.wireOp",EDGE,"E23.filletArc");var subQ11=sQuery(id+"F0.wireOp",EDGE,"E24.filletArc");Q0=makeQuery(id+"F2.boolean.opBoolean","SPLIT",FACE,{"disambiguationData":[TD([makeQuery(id+"F1.opExtrude","SWEPT_FACE",FACE,{"disambiguationData":[OSD([subQ6])]})])],"derivedFrom":makeQuery(id+"F1.opExtrude","CAP_FACE",FACE,{"disambiguationData":[OSD([subQ6,subQ8,subQ9,subQ7,subQ4,subQ3,subQ2,subQ1,subQ0,subQ5,subQ10,subQ11])],"isStart":true})});}
            var sketch = newSketch(context, id + "F16", { "sketchPlane" : qUnion([Q0])});
            skLineSegment(sketch, "E79.0", {"start": v(-80, -80) * mm, "end": v(-80, 80) * mm});
            skLineSegment(sketch, "E79.1", {"start": v(-70, 90) * mm, "end": v(70, 90) * mm});
            skArc(sketch, "E79.2", {"start": v(-70, 90) * mm, "mid": v(-77.07, 87.07) * mm, "end": v(-80, 80) * mm});
            skArc(sketch, "E79.3", {"start": v(80, 80) * mm, "mid": v(77.07, 87.07) * mm, "end": v(70, 90) * mm});
            skLineSegment(sketch, "E79.4", {"start": v(80, -80) * mm, "end": v(80, 80) * mm});
            skArc(sketch, "E79.5", {"start": v(70, -90) * mm, "mid": v(77.07, -87.07) * mm, "end": v(80, -80) * mm});
            skLineSegment(sketch, "E79.6", {"start": v(-70, -90) * mm, "end": v(70, -90) * mm});
            skArc(sketch, "E79.7", {"start": v(-80, -80) * mm, "mid": v(-77.07, -87.07) * mm, "end": v(-70, -90) * mm});
            skLineSegment(sketch, "E79.8", {"start": v(-60, 40.3) * mm, "end": v(-60, -40.3) * mm});
            skArc(sketch, "E79.9", {"start": v(-60, -40.3) * mm, "mid": v(-58.99, -44.68) * mm, "end": v(-56.15, -48.18) * mm});
            skArc(sketch, "E79.10", {"start": v(-56.15, -48.18) * mm, "mid": v(0, -67.5) * mm, "end": v(56.15, -48.18) * mm});
            skLineSegment(sketch, "E79.11", {"start": v(60, 40.3) * mm, "end": v(60, -40.3) * mm});
            skArc(sketch, "E79.12", {"start": v(56.15, -48.18) * mm, "mid": v(58.99, -44.68) * mm, "end": v(60, -40.3) * mm});
            skArc(sketch, "E79.13", {"start": v(56.15, 48.18) * mm, "mid": v(0, 67.5) * mm, "end": v(-56.15, 48.18) * mm});
            skArc(sketch, "E79.14", {"start": v(60, 40.3) * mm, "mid": v(58.99, 44.68) * mm, "end": v(56.15, 48.18) * mm});
            skArc(sketch, "E79.15", {"start": v(-56.15, 48.18) * mm, "mid": v(-58.99, 44.68) * mm, "end": v(-60, 40.3) * mm});
            skCircle(sketch, "E79.16", {"center": v(-60, 67.5) * mm, "radius": 4 * mm});
            skCircle(sketch, "E79.17", {"center": v(60, 67.5) * mm, "radius": 4 * mm});
            skCircle(sketch, "E79.18", {"center": v(60, -67.5) * mm, "radius": 4 * mm});
            skCircle(sketch, "E79.19", {"center": v(-60, -67.5) * mm, "radius": 4 * mm});
            skLineSegment(sketch, "E80", {"start": v(0, 90) * mm, "end": v(0, 120) * mm, "construction": true});
            skCircle(sketch, "E81", {"center": v(0, 120) * mm, "radius": 6 * mm});
            skArc(sketch, "E82", {"start": v(15, 120) * mm, "mid": v(0, 135) * mm, "end": v(-15, 120) * mm});
            skLineSegment(sketch, "E83", {"start": v(-15, 120) * mm, "end": v(-15, 108) * mm});
            skLineSegment(sketch, "E84", {"start": v(-15, 108) * mm, "end": v(-33, 90) * mm});
            skLineSegment(sketch, "E85", {"start": v(15, 120) * mm, "end": v(15, 108) * mm});
            skLineSegment(sketch, "E86", {"start": v(15, 108) * mm, "end": v(33, 90) * mm});
            skLineSegment(sketch, "E87", {"start": v(-80, 0) * mm, "end": v(80, 0) * mm, "construction": true});
            skLineSegment(sketch, "E88.MirrorCS", {"start": v(-15, -108) * mm, "end": v(-33, -90) * mm});
            skLineSegment(sketch, "E89.MirrorCS", {"start": v(-15, -120) * mm, "end": v(-15, -108) * mm});
            skArc(sketch, "E90.MirrorCS", {"start": v(15, -120) * mm, "mid": v(0, -135) * mm, "end": v(-15, -120) * mm});
            skCircle(sketch, "E91.MirrorC", {"center": v(0, -120) * mm, "radius": 6 * mm});
            skLineSegment(sketch, "E92.MirrorCS", {"start": v(15, -120) * mm, "end": v(15, -108) * mm});
            skLineSegment(sketch, "E93.MirrorCS", {"start": v(0, -90) * mm, "end": v(0, -120) * mm, "construction": true});
            skLineSegment(sketch, "E94.MirrorCS", {"start": v(15, -108) * mm, "end": v(33, -90) * mm});
            skSolve(sketch);
        }
        {
            var Q0;
            Q0 = qSketchRegion(id + "F16", true);
            var Q1;
            Q1=makeQuery(id+"F2.opExtrude","CAP_FACE",FACE,{"disambiguationData":[OSD([sQuery(id+"F0.wireOp",EDGE,"E12"),sQuery(id+"F0.wireOp",EDGE,"E13"),sQuery(id+"F0.wireOp",EDGE,"E14"),sQuery(id+"F0.wireOp",EDGE,"E15"),sQuery(id+"F0.wireOp",EDGE,"E17.filletArc"),sQuery(id+"F0.wireOp",EDGE,"E18.filletArc"),sQuery(id+"F0.wireOp",EDGE,"E19.filletArc"),sQuery(id+"F0.wireOp",EDGE,"E20.filletArc"),sQuery(id+"F0.wireOp",EDGE,"E25.0"),sQuery(id+"F0.wireOp",EDGE,"E25.1"),sQuery(id+"F0.wireOp",EDGE,"E25.2"),sQuery(id+"F0.wireOp",EDGE,"E25.3"),sQuery(id+"F0.wireOp",EDGE,"E25.4"),sQuery(id+"F0.wireOp",EDGE,"E25.5"),sQuery(id+"F0.wireOp",EDGE,"E25.6"),sQuery(id+"F0.wireOp",EDGE,"E25.7")])],"isStart":false});
            extrude(context, id + "F17", {"entities" : qUnion([Q0]), "endBound" : BoundingType.UP_TO_SURFACE, "depth" : 25 * mm, "endBoundEntityFace" : qUnion([Q1]), "offsetDistance" : 25 * mm});
        }
    });
